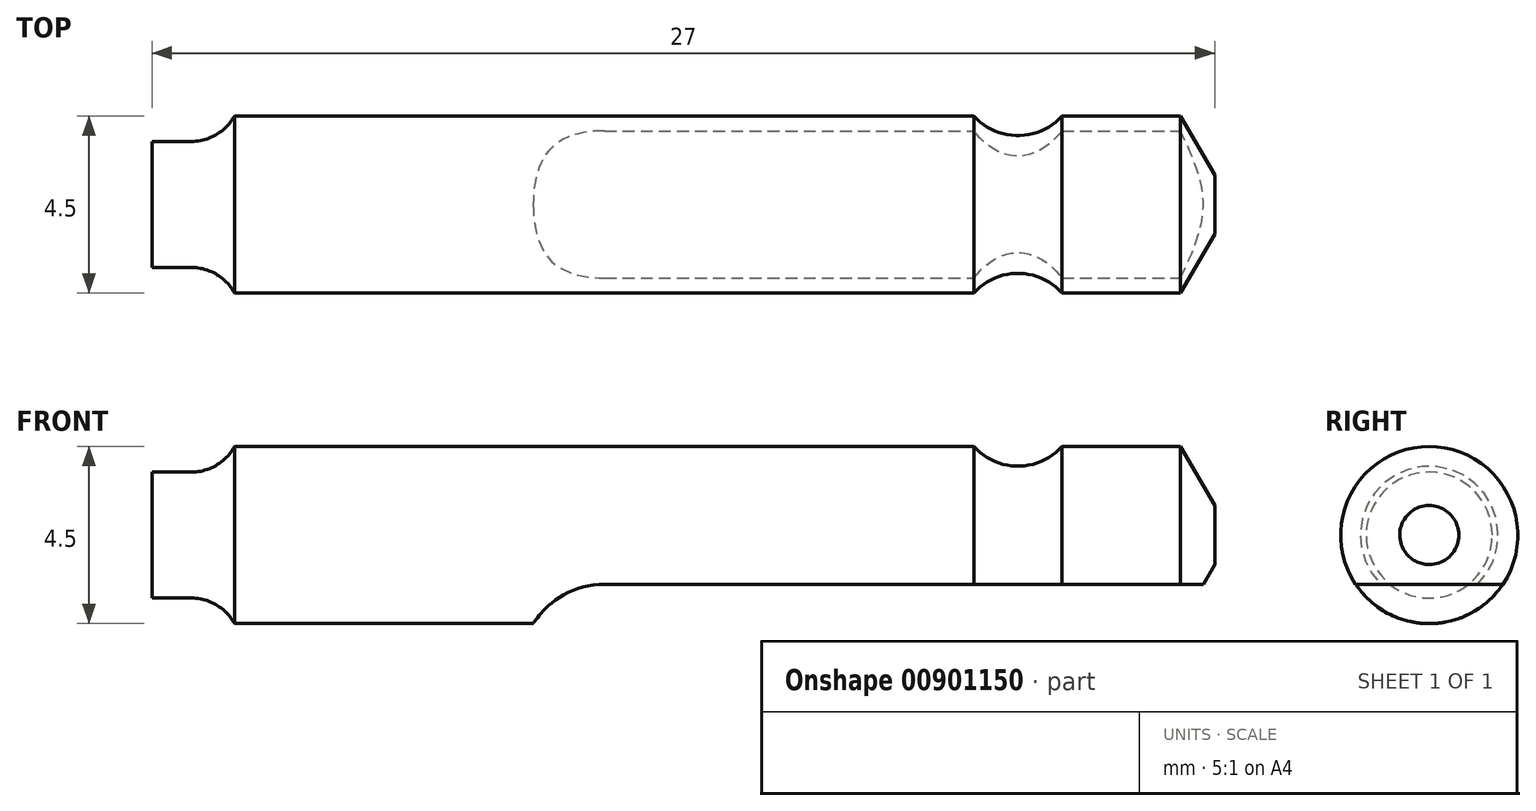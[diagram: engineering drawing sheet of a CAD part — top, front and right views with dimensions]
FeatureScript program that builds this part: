
annotation { "Feature Type Name" : "Feature", "Feature Type Description" : "" }
export const myFeature = defineFeature(function(context is Context, id is Id, definition is map)
    precondition{}
    {
        {
            var Q0;
            Q0=qCreatedBy(makeId("Front.planeOp"),FACE);
            var sketch = newSketch(context, id + "F0", { "sketchPlane" : qUnion([Q0])});
            skLineSegment(sketch, "E0", {"start": v(0, 0.85) * mm, "end": v(1, 0.85) * mm});
            skArc(sketch, "E1", {"start": v(1, 0.85) * mm, "mid": v(1.64, 1.02) * mm, "end": v(2.1, 1.5) * mm});
            skLineSegment(sketch, "E2", {"start": v(2.1, 1.5) * mm, "end": v(20.88, 1.5) * mm});
            skArc(sketch, "E3", {"start": v(20.88, 1.5) * mm, "mid": v(22, 1) * mm, "end": v(23.12, 1.5) * mm});
            skLineSegment(sketch, "E4", {"start": v(23.12, 1.5) * mm, "end": v(26.13, 1.5) * mm});
            skLineSegment(sketch, "E5", {"start": v(26.13, 1.5) * mm, "end": v(27, 0) * mm});
            skLineSegment(sketch, "E6", {"start": v(27, 0) * mm, "end": v(27, -0.75) * mm});
            skLineSegment(sketch, "E7", {"start": v(27, -0.75) * mm, "end": v(0, -0.75) * mm});
            skLineSegment(sketch, "E8", {"start": v(0, -0.75) * mm, "end": v(0, 0.85) * mm});
            skLineSegment(sketch, "E9", {"start": v(0, 7.55) * mm, "end": v(0, -6.48) * mm, "construction": true});
            skSolve(sketch);
        }
        {
            var Q0;
            Q0=makeQuery(id+"F0.imprint","IMPRINT",FACE,{"disambiguationData":[TD([[makeQuery(id+"F0.imprint","IMPRINT",EDGE,{"derivedFrom":sQuery(id+"F0.wireOp",EDGE,"E0")}),-1.0]])]});
            var Q1;
            Q1=sQuery(id+"F0.wireOp",EDGE,"E7");
            revolve(context, id + "F1", {"surfaceOperationType" : NewSurfaceOperationType.NEW, "entities" : qUnion([Q0]), "axis" : qUnion([Q1]), "revolveType" : RevolveType.FULL});
        }
        {
            var Q0;
            Q0=makeQuery(id+"F1.opRevolve","SWEPT_FACE",FACE,{"disambiguationData":[OSD([sQuery(id+"F0.wireOp",EDGE,"E6")])]});
            cPlane(context, id + "F2", {"entities" : qUnion([Q0]), "cplaneType" : CPlaneType.OFFSET, "offset" : 0 * mm, "width" : 150 * mm, "height" : 150 * mm});
        }
        {
            var Q0;
            Q0=qCreatedBy(id+"F2.planeOp",FACE);
            var sketch = newSketch(context, id + "F3", { "sketchPlane" : qUnion([Q0])});
            skLineSegment(sketch, "E10", {"start": v(0, -3) * mm, "end": v(0, 1.5) * mm, "construction": true});
            skPoint(sketch, "E11", {"position": v(0, 22.4) * mm});
            skPoint(sketch, "E12", {"position": v(0, -2) * mm});
            skLineSegment(sketch, "E13", {"start": v(0, -2) * mm, "end": v(2.38, -2) * mm});
            skLineSegment(sketch, "E14", {"start": v(2.38, -2) * mm, "end": v(2.38, -3) * mm});
            skLineSegment(sketch, "E15", {"start": v(2.38, -3) * mm, "end": v(-2.62, -3) * mm});
            skLineSegment(sketch, "E16", {"start": v(-2.62, -3) * mm, "end": v(-2.62, -2) * mm});
            skLineSegment(sketch, "E17", {"start": v(-2.62, -2) * mm, "end": v(0, -2) * mm});
            skSolve(sketch);
        }
        {
            var Q0;
            Q0=qCreatedBy(makeId("Front.planeOp"),FACE);
            var sketch = newSketch(context, id + "F4", { "sketchPlane" : qUnion([Q0])});
            skLineSegment(sketch, "E18", {"start": v(27, -2) * mm, "end": v(11.5, -2) * mm});
            skArc(sketch, "E19", {"start": v(11.5, -2) * mm, "mid": v(10.43, -2.28) * mm, "end": v(9.65, -3.06) * mm});
            skPoint(sketch, "E20", {"position": v(27, -2) * mm});
            skSolve(sketch);
        }
        {
            var Q0;
            Q0 = qSketchRegion(id + "F3", true);
            var Q1;
            Q1 = qConstructionFilter(qBodyType(qCreatedBy(id + "F4" ,EDGE), BodyType.WIRE), ConstructionObject.NO);
            sweep(context, id + "F5", {"operationType" : NewBodyOperationType.REMOVE, "profiles" : qUnion([Q0]), "path" : qUnion([Q1])});
        }
    });
